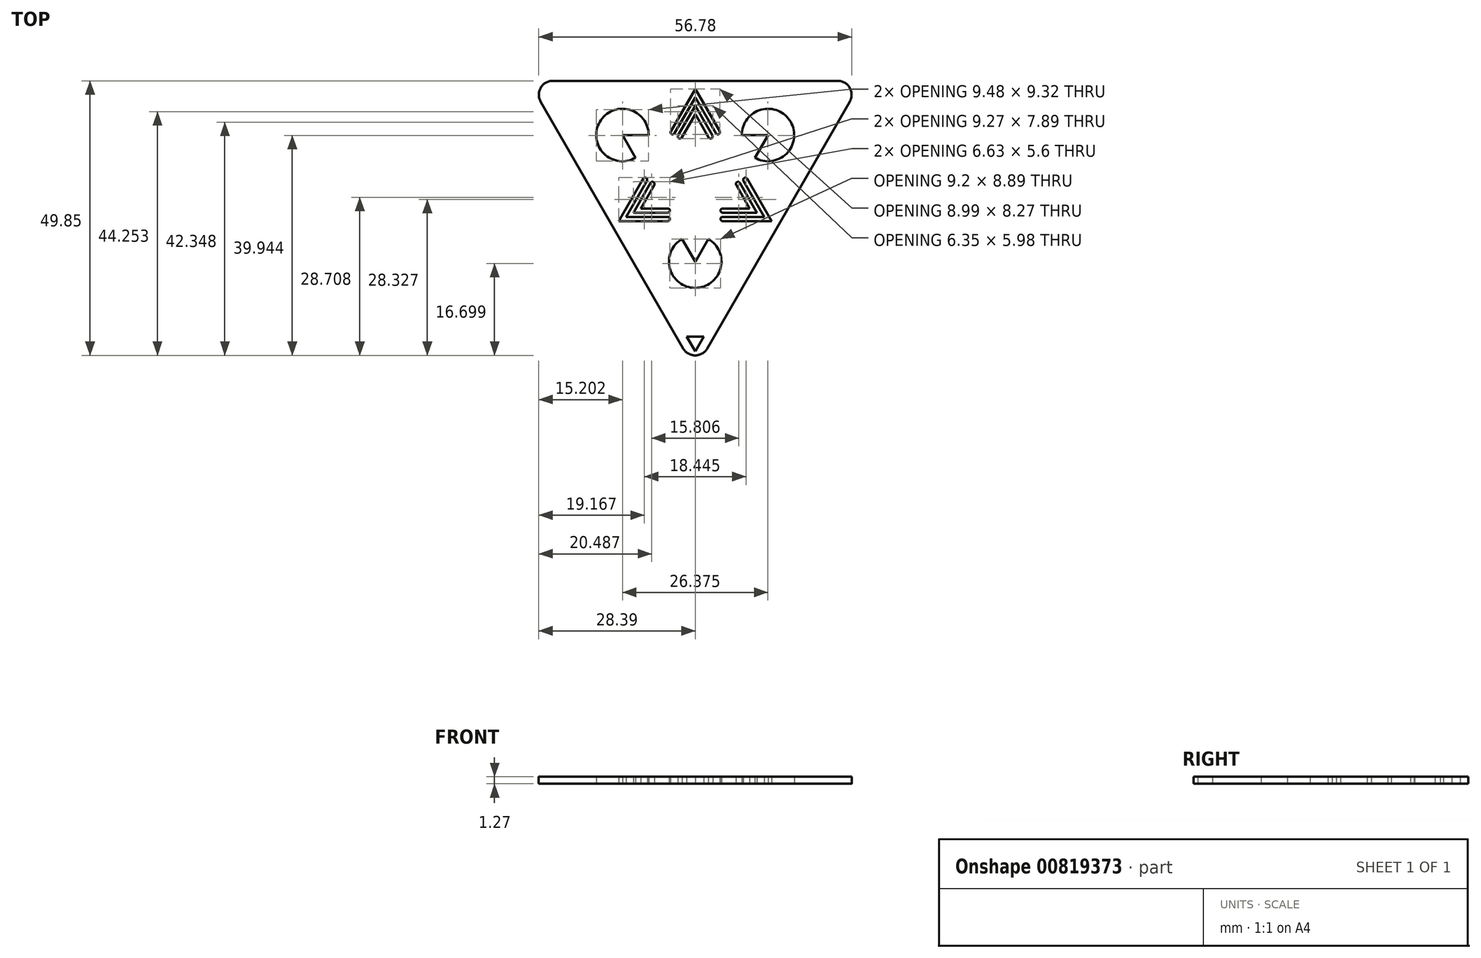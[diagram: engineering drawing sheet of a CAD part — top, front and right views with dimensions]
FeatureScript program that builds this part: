
annotation { "Feature Type Name" : "Feature", "Feature Type Description" : "" }
export const myFeature = defineFeature(function(context is Context, id is Id, definition is map)
    precondition{}
    {
        {
            var Q0;
            Q0=qCreatedBy(makeId("Top.planeOp"),FACE);
            var sketch = newSketch(context, id + "F0", { "sketchPlane" : qUnion([Q0])});
            skArc(sketch, "E0", {"start": v(-8.45, 6.99) * mm, "mid": v(-17.33, 9.37) * mm, "end": v(-10.83, 2.86) * mm});
            skArc(sketch, "E1", {"start": v(10.83, 2.86) * mm, "mid": v(17.33, 9.37) * mm, "end": v(8.45, 6.99) * mm});
            skArc(sketch, "E2", {"start": v(-2.38, -11.88) * mm, "mid": v(0, -20.76) * mm, "end": v(2.38, -11.88) * mm});
            skCircle(sketch, "E3.cCircle", {"center": v(0, -0.64) * mm, "radius": 7.24 * mm, "construction": true});
            skLineSegment(sketch, "E3.0", {"start": v(12.54, -7.87) * mm, "end": v(4.97, -7.87) * mm});
            skLineSegment(sketch, "E3.1", {"start": v(-12.54, -7.87) * mm, "end": v(-8.75, -1.32) * mm});
            skLineSegment(sketch, "E3.2", {"start": v(0, 13.84) * mm, "end": v(3.79, 7.29) * mm});
            skPoint(sketch, "E3.0.midPoint", {"position": v(0, -7.87) * mm});
            skCircle(sketch, "E4.cCircle", {"center": v(0, -0.64) * mm, "radius": 8 * mm, "construction": true});
            skLineSegment(sketch, "E4.0", {"start": v(13.86, -8.64) * mm, "end": v(4.97, -8.64) * mm});
            skLineSegment(sketch, "E4.1", {"start": v(-13.86, -8.64) * mm, "end": v(-9.41, -0.94) * mm});
            skLineSegment(sketch, "E4.2", {"start": v(0, 15.37) * mm, "end": v(4.45, 7.67) * mm});
            skPoint(sketch, "E4.0.midPoint", {"position": v(0, -8.64) * mm});
            skLineSegment(sketch, "E5", {"start": v(-4.3, 7.15) * mm, "end": v(-4.3, 7.15) * mm});
            skLineSegment(sketch, "E6", {"start": v(4.3, 7.15) * mm, "end": v(4.3, 7.15) * mm});
            skLineSegment(sketch, "E7", {"start": v(-4.59, -8.25) * mm, "end": v(-4.59, -8.25) * mm});
            skLineSegment(sketch, "E8", {"start": v(4.59, -8.25) * mm, "end": v(4.59, -8.26) * mm});
            skLineSegment(sketch, "E9", {"start": v(-8.9, -0.8) * mm, "end": v(-8.9, -0.8) * mm});
            skLineSegment(sketch, "E10", {"start": v(8.9, -0.8) * mm, "end": v(8.9, -0.8) * mm});
            skLineSegment(sketch, "E11", {"start": v(-13.2, 6.99) * mm, "end": v(-8.45, 6.99) * mm});
            skLineSegment(sketch, "E12", {"start": v(-13.2, 6.99) * mm, "end": v(-10.83, 2.86) * mm});
            skLineSegment(sketch, "E13", {"start": v(-2.38, -11.88) * mm, "end": v(0, -16) * mm});
            skLineSegment(sketch, "E14", {"start": v(0, -16) * mm, "end": v(2.38, -11.88) * mm});
            skLineSegment(sketch, "E15", {"start": v(13.2, 6.99) * mm, "end": v(8.45, 6.99) * mm});
            skLineSegment(sketch, "E16", {"start": v(13.2, 6.99) * mm, "end": v(10.83, 2.86) * mm});
            skLineSegment(sketch, "E17.trimOffspring", {"start": v(-4.44, 7.67) * mm, "end": v(0, 15.37) * mm});
            skLineSegment(sketch, "E18.trimOffspring", {"start": v(-3.79, 7.29) * mm, "end": v(0, 13.84) * mm});
            skLineSegment(sketch, "E19.trimOffspring", {"start": v(8.75, -1.32) * mm, "end": v(12.54, -7.87) * mm});
            skLineSegment(sketch, "E20.trimOffspring", {"start": v(9.41, -0.94) * mm, "end": v(13.86, -8.64) * mm});
            skLineSegment(sketch, "E21.trimOffspring", {"start": v(-4.97, -7.87) * mm, "end": v(-12.54, -7.87) * mm});
            skLineSegment(sketch, "E22.trimOffspring", {"start": v(-4.97, -8.64) * mm, "end": v(-13.86, -8.64) * mm});
            skPoint(sketch, "E23.visualSharp", {"position": v(-4.64, 7.34) * mm});
            skArc(sketch, "E23.filletArc", {"start": v(-4.44, 7.67) * mm, "mid": v(-4.48, 7.38) * mm, "end": v(-4.3, 7.15) * mm});
            skArc(sketch, "E24.filletArc", {"start": v(-4.3, 7.15) * mm, "mid": v(-4.02, 7.1) * mm, "end": v(-3.79, 7.29) * mm});
            skPoint(sketch, "E25.visualSharp", {"position": v(3.98, 6.96) * mm});
            skArc(sketch, "E25.filletArc", {"start": v(3.79, 7.29) * mm, "mid": v(4.02, 7.1) * mm, "end": v(4.3, 7.15) * mm});
            skPoint(sketch, "E26.visualSharp", {"position": v(4.64, 7.34) * mm});
            skArc(sketch, "E26.filletArc", {"start": v(4.3, 7.15) * mm, "mid": v(4.48, 7.38) * mm, "end": v(4.45, 7.67) * mm});
            skPoint(sketch, "E27.visualSharp", {"position": v(-4.59, -7.87) * mm});
            skArc(sketch, "E27.filletArc", {"start": v(-4.59, -8.25) * mm, "mid": v(-4.7, -7.99) * mm, "end": v(-4.97, -7.87) * mm});
            skPoint(sketch, "E28.visualSharp", {"position": v(-4.59, -8.64) * mm});
            skArc(sketch, "E28.filletArc", {"start": v(-4.97, -8.64) * mm, "mid": v(-4.7, -8.52) * mm, "end": v(-4.59, -8.25) * mm});
            skPoint(sketch, "E29.visualSharp", {"position": v(4.59, -8.64) * mm});
            skArc(sketch, "E29.filletArc", {"start": v(4.59, -8.26) * mm, "mid": v(4.7, -8.52) * mm, "end": v(4.97, -8.64) * mm});
            skPoint(sketch, "E30.visualSharp", {"position": v(4.59, -7.87) * mm});
            skArc(sketch, "E30.filletArc", {"start": v(4.97, -7.87) * mm, "mid": v(4.7, -7.99) * mm, "end": v(4.59, -8.25) * mm});
            skPoint(sketch, "E31.visualSharp", {"position": v(8.56, -0.99) * mm});
            skArc(sketch, "E31.filletArc", {"start": v(8.9, -0.8) * mm, "mid": v(8.72, -1.03) * mm, "end": v(8.75, -1.32) * mm});
            skPoint(sketch, "E32.visualSharp", {"position": v(9.22, -0.6) * mm});
            skArc(sketch, "E32.filletArc", {"start": v(9.41, -0.94) * mm, "mid": v(9.18, -0.76) * mm, "end": v(8.9, -0.8) * mm});
            skPoint(sketch, "E33.visualSharp", {"position": v(-9.22, -0.6) * mm});
            skArc(sketch, "E33.filletArc", {"start": v(-8.9, -0.8) * mm, "mid": v(-9.18, -0.76) * mm, "end": v(-9.41, -0.94) * mm});
            skPoint(sketch, "E34.visualSharp", {"position": v(-8.56, -0.99) * mm});
            skArc(sketch, "E34.filletArc", {"start": v(-8.75, -1.32) * mm, "mid": v(-8.72, -1.03) * mm, "end": v(-8.9, -0.8) * mm});
            skLineSegment(sketch, "E35.0", {"start": v(-30.25, 16.83) * mm, "end": v(30.25, 16.83) * mm});
            skLineSegment(sketch, "E35.1", {"start": v(30.25, 16.83) * mm, "end": v(0, -35.56) * mm});
            skLineSegment(sketch, "E35.2", {"start": v(0, -35.56) * mm, "end": v(-30.25, 16.83) * mm});
            skPoint(sketch, "E35.0.midPoint", {"position": v(0, 16.83) * mm});
            skPoint(sketch, "E36.0.midPoint", {"position": v(0, -10.97) * mm});
            skCircle(sketch, "E37.cCircle", {"center": v(0, -0.64) * mm, "radius": 6.48 * mm, "construction": true});
            skLineSegment(sketch, "E37.0", {"start": v(-11.22, -7.11) * mm, "end": v(-8.1, -1.7) * mm});
            skLineSegment(sketch, "E37.1", {"start": v(0, 12.32) * mm, "end": v(3.13, 6.9) * mm});
            skPoint(sketch, "E37.0.midPoint", {"position": v(-5.6, 2.6) * mm});
            skCircle(sketch, "E38.cCircle", {"center": v(0, -0.63) * mm, "radius": 5.72 * mm, "construction": true});
            skLineSegment(sketch, "E38.0", {"start": v(0, 10.8) * mm, "end": v(2.47, 6.53) * mm});
            skLineSegment(sketch, "E38.1", {"start": v(9.9, -6.35) * mm, "end": v(4.97, -6.35) * mm});
            skLineSegment(sketch, "E38.2", {"start": v(-9.9, -6.35) * mm, "end": v(-7.43, -2.08) * mm});
            skPoint(sketch, "E38.0.midPoint", {"position": v(4.95, 2.22) * mm});
            skLineSegment(sketch, "E39", {"start": v(-9.41, -0.94) * mm, "end": v(-8.75, -1.32) * mm, "construction": true});
            skPoint(sketch, "E39.endSnap0", {"position": v(0, -7.11) * mm});
            skLineSegment(sketch, "E40", {"start": v(0, -6.37) * mm, "end": v(7.43, -2.08) * mm, "construction": true});
            skLineSegment(sketch, "E41", {"start": v(-4.44, 7.67) * mm, "end": v(-3.79, 7.29) * mm, "construction": true});
            skLineSegment(sketch, "E42", {"start": v(0, 5.1) * mm, "end": v(2.08, 6.3) * mm, "construction": true});
            skLineSegment(sketch, "E43.trimOffspring", {"start": v(8.1, -1.7) * mm, "end": v(11.22, -7.11) * mm});
            skLineSegment(sketch, "E44.trimOffspring", {"start": v(7.43, -2.08) * mm, "end": v(9.9, -6.35) * mm});
            skLineSegment(sketch, "E45.trimOffspring", {"start": v(-2.47, 6.53) * mm, "end": v(0, 10.8) * mm});
            skLineSegment(sketch, "E46.trimOffspring", {"start": v(-3.13, 6.9) * mm, "end": v(0, 12.32) * mm});
            skArc(sketch, "E47", {"start": v(-8.1, -1.7) * mm, "mid": v(-7.57, -1.56) * mm, "end": v(-7.43, -2.08) * mm});
            skArc(sketch, "E48", {"start": v(8.1, -1.7) * mm, "mid": v(7.57, -1.56) * mm, "end": v(7.43, -2.08) * mm});
            skLineSegment(sketch, "E49.trimOffspring", {"start": v(8.1, -1.7) * mm, "end": v(9.41, -0.94) * mm, "construction": true});
            skLineSegment(sketch, "E50.trimOffspring", {"start": v(-7.43, -2.08) * mm, "end": v(0, -6.37) * mm, "construction": true});
            skArc(sketch, "E51", {"start": v(3.13, 6.9) * mm, "mid": v(2.99, 6.39) * mm, "end": v(2.47, 6.53) * mm});
            skArc(sketch, "E52", {"start": v(-2.47, 6.53) * mm, "mid": v(-2.99, 6.39) * mm, "end": v(-3.13, 6.9) * mm});
            skLineSegment(sketch, "E53.trimOffspring", {"start": v(-2.47, 6.53) * mm, "end": v(0, 5.1) * mm, "construction": true});
            skLineSegment(sketch, "E54.trimOffspring", {"start": v(3.13, 6.9) * mm, "end": v(4.45, 7.67) * mm, "construction": true});
            skLineSegment(sketch, "E55", {"start": v(-4.97, -8.64) * mm, "end": v(-4.97, -7.87) * mm, "construction": true});
            skLineSegment(sketch, "E56", {"start": v(4.97, -8.64) * mm, "end": v(4.97, -7.11) * mm, "construction": true});
            skLineSegment(sketch, "E57.trimOffspring", {"start": v(-4.97, -6.35) * mm, "end": v(-9.9, -6.35) * mm});
            skLineSegment(sketch, "E58.trimOffspring", {"start": v(0.04, -6.35) * mm, "end": v(-0.04, -6.35) * mm});
            skLineSegment(sketch, "E59.trimOffspring", {"start": v(-4.97, -7.11) * mm, "end": v(-11.22, -7.11) * mm});
            skArc(sketch, "E60", {"start": v(-4.97, -6.35) * mm, "mid": v(-4.59, -6.73) * mm, "end": v(-4.97, -7.11) * mm});
            skLineSegment(sketch, "E61", {"start": v(4.97, -7.11) * mm, "end": v(11.22, -7.11) * mm});
            skArc(sketch, "E62", {"start": v(4.97, -6.35) * mm, "mid": v(4.59, -6.73) * mm, "end": v(4.97, -7.11) * mm});
            skLineSegment(sketch, "E63.trimOffspring", {"start": v(4.97, -6.35) * mm, "end": v(4.97, -2.57) * mm, "construction": true});
            skLineSegment(sketch, "E64.trimOffspring", {"start": v(-4.97, -6.35) * mm, "end": v(-4.97, -1.6) * mm, "construction": true});
            skCircle(sketch, "E65.cCircle", {"center": v(0, -30.48) * mm, "radius": 0.89 * mm, "construction": true});
            skLineSegment(sketch, "E65.0", {"start": v(1.54, -29.6) * mm, "end": v(0, -32.26) * mm});
            skLineSegment(sketch, "E65.1", {"start": v(0, -32.26) * mm, "end": v(-1.54, -29.6) * mm});
            skLineSegment(sketch, "E65.2", {"start": v(-1.54, -29.6) * mm, "end": v(1.54, -29.6) * mm});
            skPoint(sketch, "E65.0.midPoint", {"position": v(0.77, -30.92) * mm});
            skSolve(sketch);
        }
        {
            var Q0;
            Q0=makeQuery(id+"F0.imprint","IMPRINT",FACE,{"disambiguationData":[TD([[makeQuery(id+"F0.imprint","IMPRINT",EDGE,{"derivedFrom":sQuery(id+"F0.wireOp",EDGE,"E0")}),-1.0]])]});
            extrude(context, id + "F1", {"entities" : qUnion([Q0]), "depth" : 1.27 * mm, "offsetDistance" : 25.4 * mm});
        }
        {
            var Q0;
            Q0=makeQuery(id+"F1.opExtrude","SWEPT_EDGE",EDGE,{"disambiguationData":[OSD([sQuery(id+"F0.wireOp",EDGE,"E35.0"),sQuery(id+"F0.wireOp",EDGE,"E35.2")])]});
            var Q1;
            Q1=makeQuery(id+"F1.opExtrude","SWEPT_EDGE",EDGE,{"disambiguationData":[OSD([sQuery(id+"F0.wireOp",EDGE,"E35.0"),sQuery(id+"F0.wireOp",EDGE,"E35.1")])]});
            var Q2;
            Q2=makeQuery(id+"F1.opExtrude","SWEPT_EDGE",EDGE,{"disambiguationData":[OSD([sQuery(id+"F0.wireOp",EDGE,"E35.1"),sQuery(id+"F0.wireOp",EDGE,"E35.2")])]});
            fillet(context, id + "F2", {"entities" : qUnion([Q0, Q1, Q2]), "radius" : 2.54 * mm, "tangentPropagation" : true, "allowEdgeOverflow" : false});
        }
    });
